# Revit family: QF_ELECTROLUXPROFESSIONAL_588205_MAKCEADDAO
name_source: partatom
category: Specialty Equipment
units: mm (PartAtom-declared; Revit-internal decimal feet)

## family parameters
Always vertical = Yes
Cut with Voids When Loaded = No
Enable Cutting in Views = No
Maintain Annotation Orientation = No
Part Type = Normal
Room Calculation Point = No
Round Connector Dimension = Use Diameter
Shared = No
Work Plane-Based = No

## types (1)
- QF_ELECTROLUXPROFESSIONAL_588205_MAKCEADDAO
    Cold Water Connection Height = 0 mm  [stored 0 ft]
    Cold Water Maximum Pressure = 0.00 psi
    Cold Water Minimum Pressure = 0.00 psi
    Cold Water Size = 1"
    Conn Conduit = Yes
    Default Elevation = 0 mm  [stored 0 ft]
    Description = EL.PASTA COOKER,1X24.5L,1-SIDE,400X800X700
    Direct Waste Size = 1"
    Electrical Remarks = 400 V/3N ph/50/60 Hz
    HP = 8 HP
    Indirect Waste Connection Height = 0 mm  [stored 0 ft]
    Indirect Waste Size = 1"
    Manufacturer = ELECTROLUX
    Max Overcurrent Protection = 0 A
    Min Ckt Ampacity = 0 A
    Model = 588205
    Phase = 3
    Volts = 400 V
    Watts = 6000 W
    Weight in Pounds = 138.89

note: [stored X ft] marks values corroborated as IEEE doubles in the binary element streams (Revit-internal decimal feet)

## geometry (parser evidence)
native form markers: Blend x8, Sweep x11
no freeform markers — native parametric forms only
